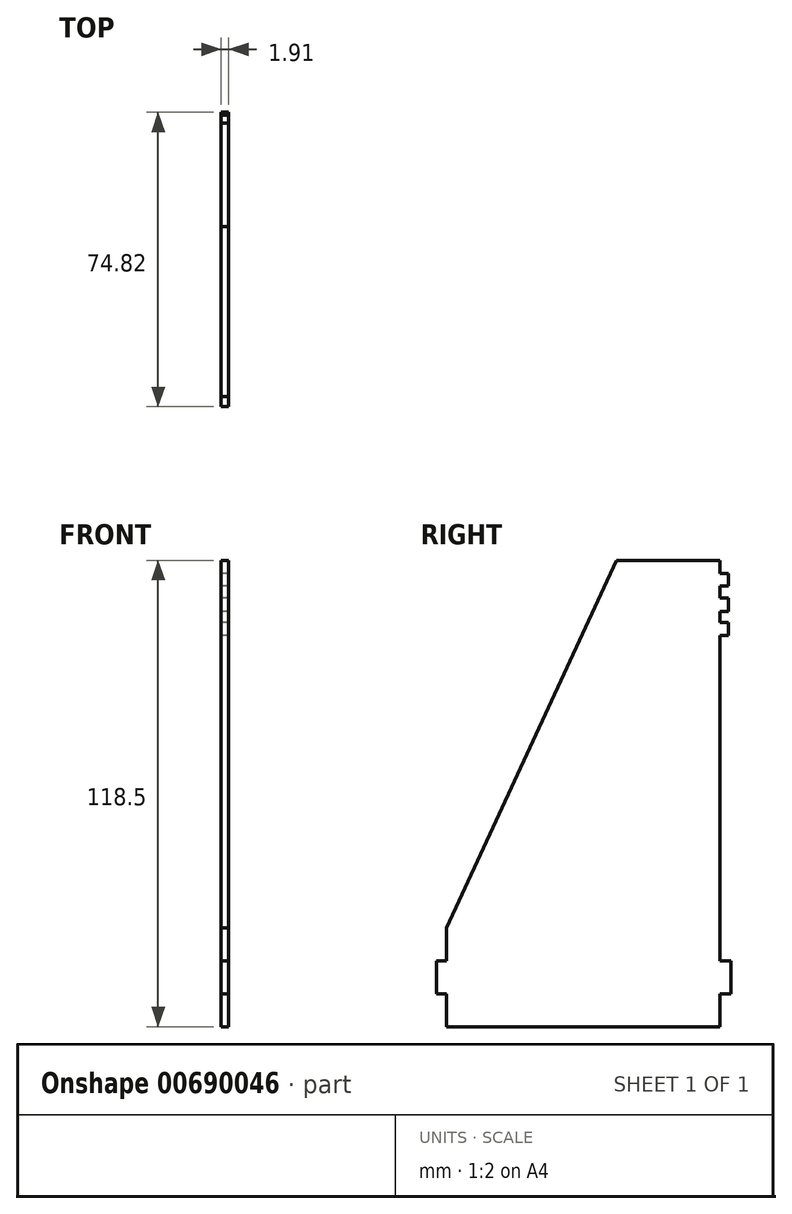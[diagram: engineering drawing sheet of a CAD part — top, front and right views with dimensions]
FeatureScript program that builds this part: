
annotation { "Feature Type Name" : "Feature", "Feature Type Description" : "" }
export const myFeature = defineFeature(function(context is Context, id is Id, definition is map)
    precondition{}
    {
        {
            var Q0;
            Q0=qCreatedBy(makeId("Right.planeOp"),FACE);
            var sketch = newSketch(context, id + "F0", { "sketchPlane" : qUnion([Q0])});
            skLineSegment(sketch, "E0", {"start": v(10.5, 60.06) * mm, "end": v(-15.78, 60.06) * mm});
            skLineSegment(sketch, "E1", {"start": v(-15.78, 60.06) * mm, "end": v(-58.96, -33.34) * mm});
            skLineSegment(sketch, "E2", {"start": v(-58.96, -33.34) * mm, "end": v(-58.96, -41.7) * mm});
            skLineSegment(sketch, "E3", {"start": v(-58.96, -41.7) * mm, "end": v(-61.52, -41.7) * mm});
            skLineSegment(sketch, "E4", {"start": v(-61.52, -41.7) * mm, "end": v(-61.52, -50.07) * mm});
            skLineSegment(sketch, "E5", {"start": v(-61.52, -50.07) * mm, "end": v(-58.96, -50.07) * mm});
            skLineSegment(sketch, "E6", {"start": v(-58.96, -50.07) * mm, "end": v(-58.96, -58.44) * mm});
            skLineSegment(sketch, "E7", {"start": v(-58.96, -58.44) * mm, "end": v(10.5, -58.44) * mm});
            skLineSegment(sketch, "E8", {"start": v(10.5, -58.44) * mm, "end": v(10.5, -50.07) * mm});
            skLineSegment(sketch, "E9", {"start": v(10.5, -50.07) * mm, "end": v(13.3, -50.07) * mm});
            skLineSegment(sketch, "E10", {"start": v(13.3, -50.07) * mm, "end": v(13.3, -41.7) * mm});
            skLineSegment(sketch, "E11", {"start": v(13.3, -41.7) * mm, "end": v(10.5, -41.7) * mm});
            skLineSegment(sketch, "E12", {"start": v(10.5, -41.7) * mm, "end": v(10.5, 40.9) * mm});
            skLineSegment(sketch, "E13", {"start": v(10.5, 40.9) * mm, "end": v(12.62, 40.9) * mm});
            skLineSegment(sketch, "E14", {"start": v(12.62, 40.9) * mm, "end": v(12.62, 44.3) * mm});
            skLineSegment(sketch, "E15", {"start": v(12.62, 44.3) * mm, "end": v(10.5, 44.3) * mm});
            skLineSegment(sketch, "E16", {"start": v(10.5, 44.3) * mm, "end": v(10.5, 47.05) * mm});
            skLineSegment(sketch, "E17", {"start": v(10.5, 47.05) * mm, "end": v(12.62, 47.05) * mm});
            skLineSegment(sketch, "E18", {"start": v(12.62, 47.05) * mm, "end": v(12.62, 50.54) * mm});
            skLineSegment(sketch, "E19", {"start": v(12.62, 50.54) * mm, "end": v(10.5, 50.54) * mm});
            skLineSegment(sketch, "E20", {"start": v(10.5, 50.54) * mm, "end": v(10.5, 53.56) * mm});
            skLineSegment(sketch, "E21", {"start": v(10.5, 53.56) * mm, "end": v(12.62, 53.56) * mm});
            skLineSegment(sketch, "E22", {"start": v(12.62, 56.7) * mm, "end": v(10.5, 56.7) * mm});
            skLineSegment(sketch, "E23", {"start": v(10.5, 56.7) * mm, "end": v(10.5, 60.06) * mm});
            skLineSegment(sketch, "E24", {"start": v(12.62, 56.7) * mm, "end": v(12.62, 53.56) * mm});
            skSolve(sketch);
        }
        {
            var Q0;
            Q0=makeQuery(id+"F0.imprint","IMPRINT",FACE,{"disambiguationData":[TD([[makeQuery(id+"F0.imprint","IMPRINT",EDGE,{"derivedFrom":sQuery(id+"F0.wireOp",EDGE,"E0")}),1.0]])]});
            extrude(context, id + "F1", {"entities" : qUnion([Q0]), "depth" : 1.9 * mm, "offsetDistance" : 25.4 * mm});
        }
    });
